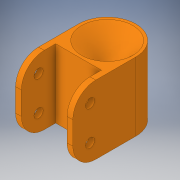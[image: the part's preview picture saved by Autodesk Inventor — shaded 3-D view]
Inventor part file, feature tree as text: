
AUTODESK INVENTOR PART (.ipt)
format: ipt  version: 2017 SP1 (Build 210196100, 196)  size: 235,008 bytes
history: native  units: in
note: dims shown in document units (in); Inventor stores cm internally (conversion verified against a paired STEP export)
features: sketch x5, extrude x2, loft x1, fillet x1, projected_geometry x1
ambient origin geometry x8: Origin, YZ Plane, XZ Plane, XY Plane, X Axis, Y Axis, Z Axis, Center Point
bodies: Solid1 (feature_tree)
feature tree (10):
  extrude  "Extrusion1"  Depth=1.5in TaperAngle=0.0deg
  loft  "Loft1"
  fillet  "Fillet1"  Radius=1.125in
  extrude  "Extrusion2"  TaperAngle=0.0deg  [1 undecoded]
  sketch  "Sketch1"  dims[d0=1.25in d1=1.5in d2=0.0in]
  sketch  "Sketch2"  dims[d3=0.25in d4=1.125in d5=1.125in]
  sketch  "Sketch3"  dims[d6=0.0in d7=90.0deg d8=0.0in d9=90.0deg]
  sketch  "Sketch4"  dims[d10=0.0in d11=90.0deg]
  sketch  "Sketch5"  dims[d12=0.625in d13=1.0in d14=0.75in d15=0.5in d16=0.2in d17=0.375in d18=0.75in d19=1.5in d20=0.0in]
  projected_geometry  "Projected Loop1"
note: 1 required parameter value undecoded (feature->parameter linkage not recoverable at this tier; creation-order binding heuristic only, values carry confidence <= 0.55)
